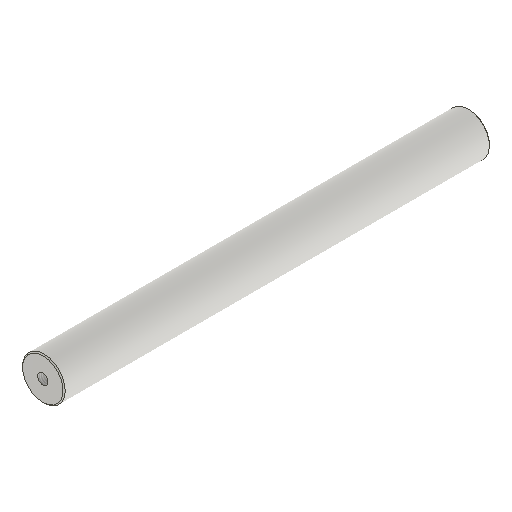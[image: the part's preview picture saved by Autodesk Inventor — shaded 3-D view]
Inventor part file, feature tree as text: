
AUTODESK INVENTOR PART (.ipt)
format: ipt  version: 2025.2 (Build 292293000, 293)  size: 109,568 bytes
history: native  units: in
note: dims shown in document units (in); Inventor stores cm internally (conversion verified against a paired STEP export)
features: sketch x2, revolve x1, hole x1, chamfer x1
ambient origin geometry x8: Origin, YZ Plane, XZ Plane, XY Plane, X Axis, Y Axis, Z Axis, Center Point
bodies: Solid1 (feature_tree)
feature tree (5):
  revolve  "Revolution1"  [1 undecoded]
  hole  "Hole1"  [1 undecoded]
  chamfer  "Chamfer1"  [1 undecoded]
  sketch  "Sketch1"  dims[d0=0.7874in d1=7.874in]
  sketch  "Sketch2"  dims[d2=90.0deg d3=0.1936in d4=0.5906in d5=0.1575in d6=0.0787in d7=90.0deg d8=0.7874in d9=0.8108in d10=0.0197in d11=0.0787in d12=45.0deg]
note: 3 required parameter values undecoded (feature->parameter linkage not recoverable at this tier; creation-order binding heuristic only, values carry confidence <= 0.55)